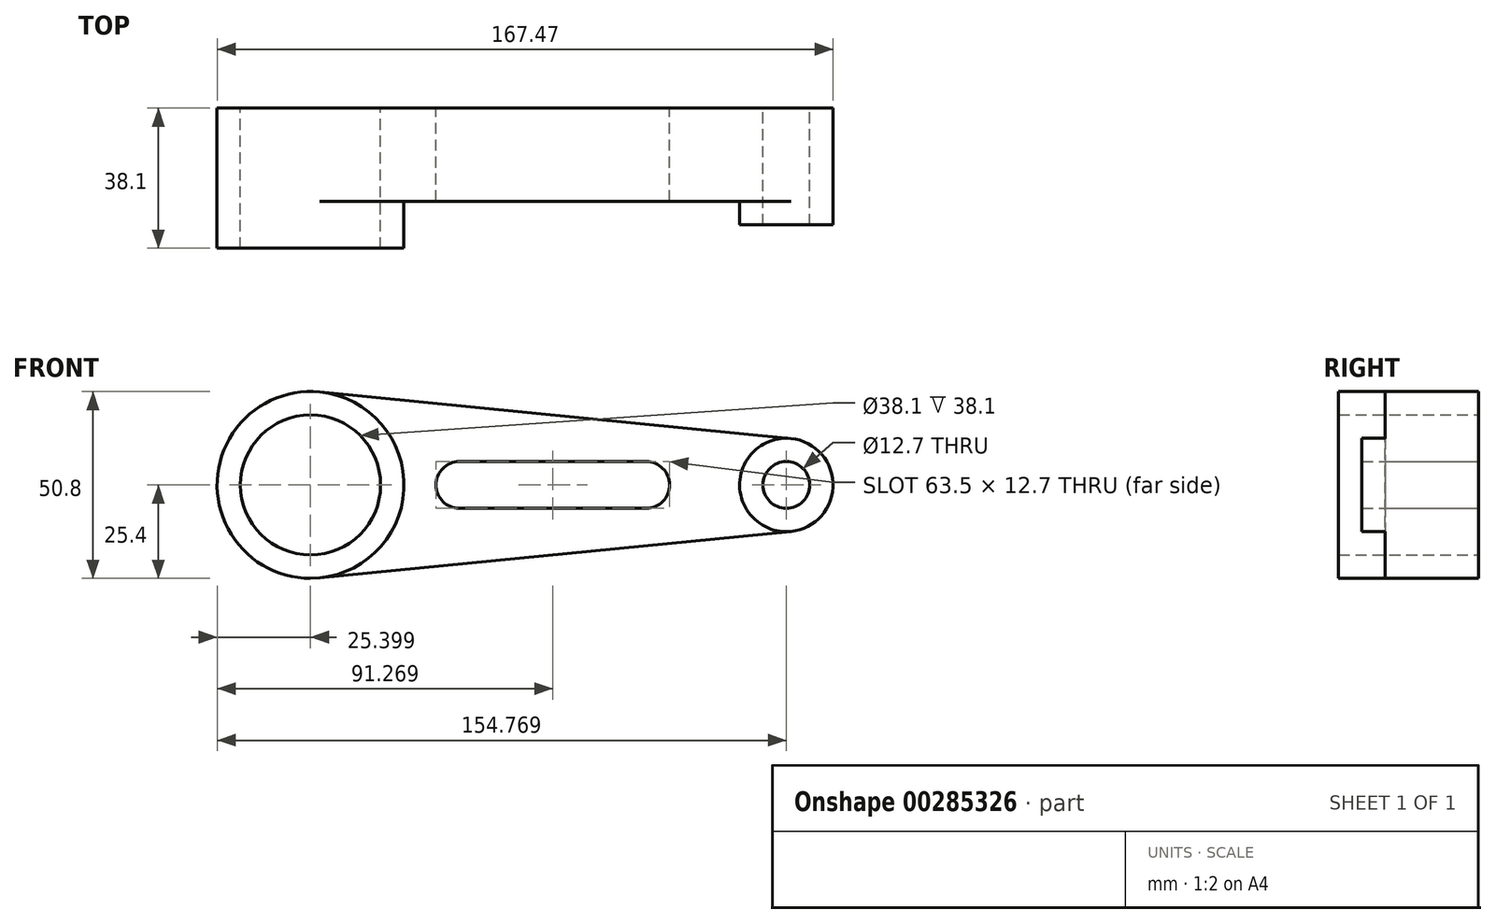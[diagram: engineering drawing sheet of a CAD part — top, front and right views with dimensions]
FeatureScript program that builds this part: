
annotation { "Feature Type Name" : "Feature", "Feature Type Description" : "" }
export const myFeature = defineFeature(function(context is Context, id is Id, definition is map)
    precondition{}
    {
        {
            var Q0;
            Q0=qCreatedBy(makeId("Front.planeOp"),FACE);
            var sketch = newSketch(context, id + "F0", { "sketchPlane" : qUnion([Q0])});
            skCircle(sketch, "E0", {"center": v(-58.37, 0) * mm, "radius": 25.4 * mm});
            skCircle(sketch, "E1", {"center": v(-58.37, 0) * mm, "radius": 19.05 * mm});
            skCircle(sketch, "E2", {"center": v(71, 0) * mm, "radius": 6.35 * mm});
            skCircle(sketch, "E3", {"center": v(71, 0) * mm, "radius": 12.7 * mm});
            skLineSegment(sketch, "E4", {"start": v(-55.88, 25.28) * mm, "end": v(72.25, 12.64) * mm});
            skLineSegment(sketch, "E5", {"start": v(-55.88, -25.28) * mm, "end": v(72.25, -12.64) * mm});
            skCircle(sketch, "E6", {"center": v(-17.9, 0) * mm, "radius": 6.35 * mm});
            skCircle(sketch, "E7", {"center": v(32.9, 0) * mm, "radius": 6.35 * mm});
            skLineSegment(sketch, "E8", {"start": v(-17.9, 6.35) * mm, "end": v(32.9, 6.35) * mm});
            skLineSegment(sketch, "E9", {"start": v(32.9, -6.35) * mm, "end": v(-17.9, -6.35) * mm});
            skLineSegment(sketch, "E10", {"start": v(32.9, 0) * mm, "end": v(71, 0) * mm, "construction": true});
            skSolve(sketch);
        }
        {
            var Q0;
            Q0=makeQuery(id+"F0.imprint","IMPRINT",FACE,{"disambiguationData":[TD([[makeQuery(id+"F0.imprint","IMPRINT",EDGE,{"derivedFrom":sQuery(id+"F0.wireOp",EDGE,"E1")}),-1.0]])]});
            extrude(context, id + "F1", {"entities" : qUnion([Q0]), "depth" : 38.1 * mm});
        }
        {
            var Q0;
            {var subQ1=sQuery(id+"F0.wireOp",EDGE,"E4");Q0=makeQuery(id+"F0.imprint","IMPRINT",FACE,{"disambiguationData":[TD([[makeQuery(id+"F0.imprint","IMPRINT",EDGE,{"derivedFrom":subQ1}),-1.0]])]});}
            extrude(context, id + "F2", {"entities" : qUnion([Q0]), "operationType" : NewBodyOperationType.ADD, "depth" : 25.4 * mm});
        }
        {
            var Q0;
            Q0=makeQuery(id+"F0.imprint","IMPRINT",FACE,{"disambiguationData":[TD([[makeQuery(id+"F0.imprint","IMPRINT",EDGE,{"derivedFrom":sQuery(id+"F0.wireOp",EDGE,"E2")}),-1.0]])]});
            extrude(context, id + "F3", {"entities" : qUnion([Q0]), "operationType" : NewBodyOperationType.ADD, "depth" : 31.75 * mm});
        }
    });
